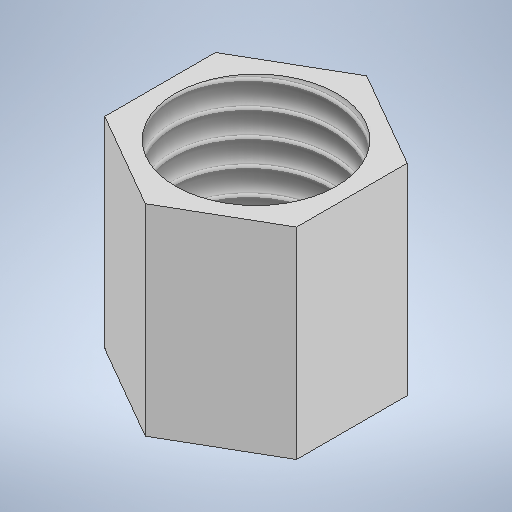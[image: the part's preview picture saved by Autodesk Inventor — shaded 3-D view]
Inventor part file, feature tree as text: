
AUTODESK INVENTOR PART (.ipt)
format: ipt  version: 2025.1 (Build 291241000, 241)  size: 271,360 bytes
history: native  units: mm
features: sketch x3, hole x2, extrude x1, thread x1
ambient origin geometry x8: Origin, YZ Plane, XZ Plane, XY Plane, X Axis, Y Axis, Z Axis, Center Point
bodies: Solid1 (feature_tree)
feature tree (7):
  extrude  "Extrusion1"  Depth=10.0mm TaperAngle=0.0deg
  hole  "Hole1"  [1 undecoded]
  thread  "Thread2"  [1 undecoded]
  hole  "Hole2"  [1 undecoded]
  sketch  "Sketch1"  dims[d0=11.0mm d1=10.0mm d2=0.0mm]
  sketch  "Sketch3"  dims[d3=8.0mm d4=16.0mm d5=8.0mm d6=7.0mm d7=90.0deg d8=7.0mm d9=0.0mm d12=15.0mm d13=0.0mm]
  sketch  "Sketch4"  dims[d14=5.0mm d15=6.0mm d16=4.0mm d17=2.0mm d18=90.0deg d19=5.0mm d20=0.0mm]
note: 3 required parameter values undecoded (feature->parameter linkage not recoverable at this tier; creation-order binding heuristic only, values carry confidence <= 0.55)
